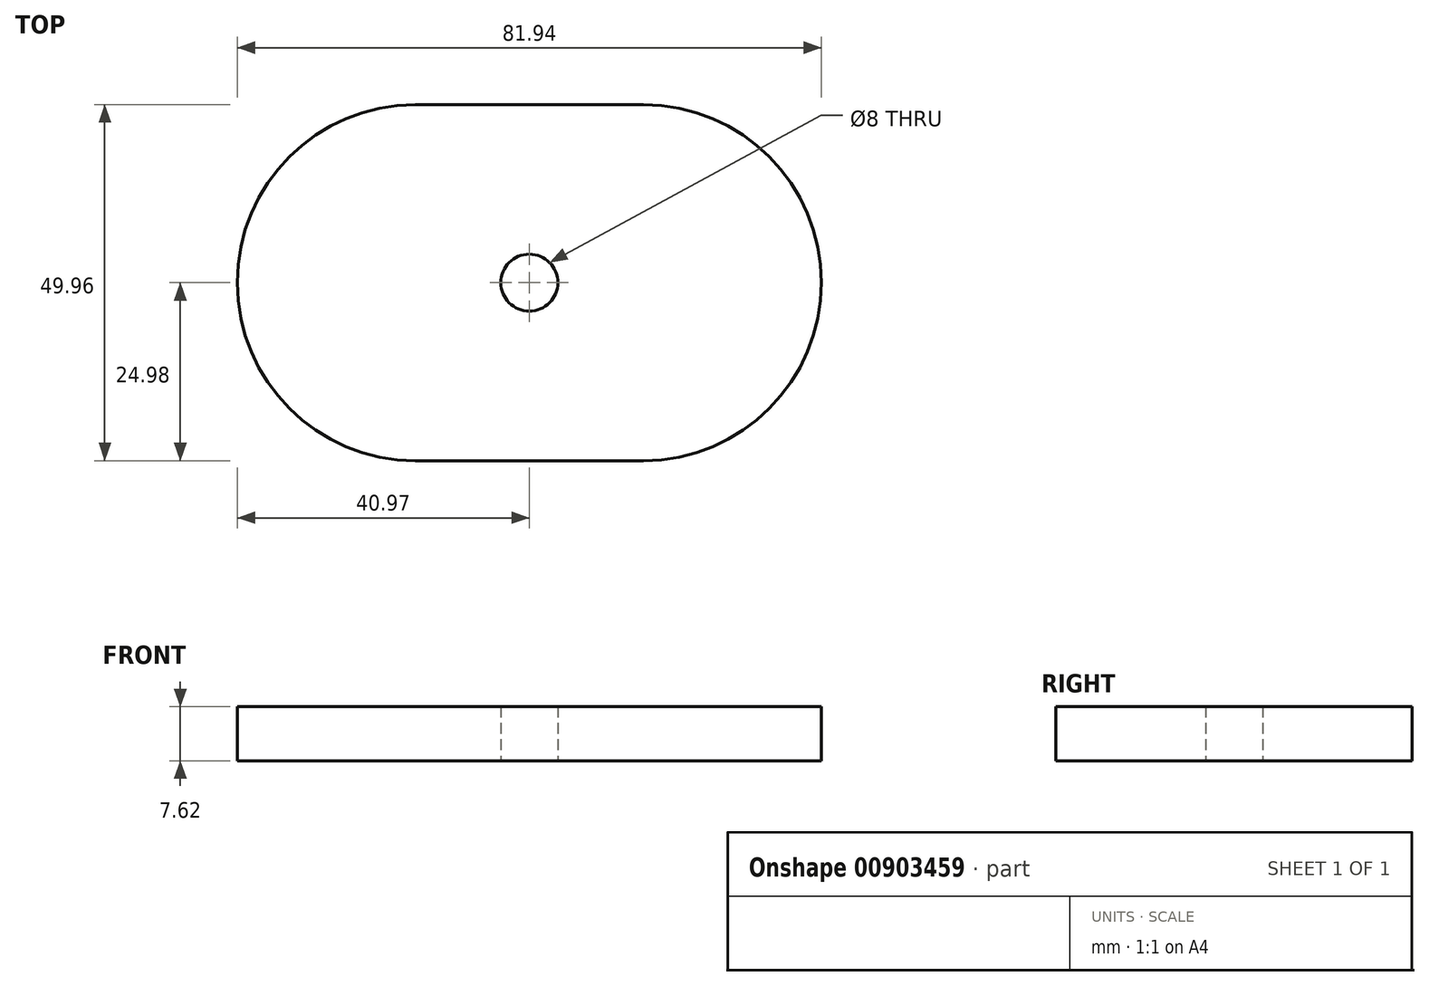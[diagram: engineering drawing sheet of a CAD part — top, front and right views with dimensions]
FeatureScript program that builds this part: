
annotation { "Feature Type Name" : "Feature", "Feature Type Description" : "" }
export const myFeature = defineFeature(function(context is Context, id is Id, definition is map)
    precondition{}
    {
        {
            var Q0;
            Q0=qCreatedBy(makeId("Top.planeOp"),FACE);
            var sketch = newSketch(context, id + "F0", { "sketchPlane" : qUnion([Q0])});
            skArc(sketch, "E0", {"start": v(-15.99, 24.98) * mm, "mid": v(-40.97, 0) * mm, "end": v(-15.99, -24.98) * mm});
            skArc(sketch, "E1", {"start": v(15.99, -24.98) * mm, "mid": v(40.97, 0) * mm, "end": v(15.99, 24.98) * mm});
            skLineSegment(sketch, "E2", {"start": v(-15.99, 24.98) * mm, "end": v(15.99, 24.98) * mm});
            skLineSegment(sketch, "E3", {"start": v(-15.99, -24.98) * mm, "end": v(15.99, -24.98) * mm});
            skPoint(sketch, "E4", {"position": v(-40.97, 0) * mm});
            skPoint(sketch, "E5", {"position": v(40.97, 0) * mm});
            skCircle(sketch, "E6", {"center": v(0, 0) * mm, "radius": 4 * mm});
            skSolve(sketch);
        }
        {
            var Q0;
            Q0 = qSketchRegion(id + "F0", true);
            extrude(context, id + "F1", {"entities" : qUnion([Q0]), "depth" : 7.62 * mm, "offsetDistance" : 25.4 * mm});
        }
    });
